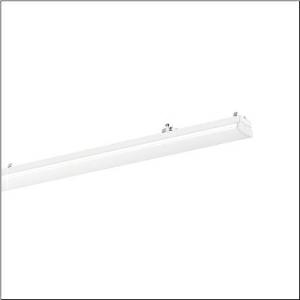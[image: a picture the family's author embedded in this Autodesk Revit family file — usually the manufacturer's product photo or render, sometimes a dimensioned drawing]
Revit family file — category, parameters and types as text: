
# Revit family: licross_21_recessed_opal_mo_52tl1ddn445g
name_source: partatom
category: Lighting Fixtures
units: mm (PartAtom-declared; Revit-internal decimal feet)

## family parameters
Cut with Voids When Loaded = No
Host = Face
Light Source = No
Part Type = Normal
Room Calculation Point = No
Round Connector Dimension = Use Diameter
Shared = No

## types (1)
- --- (1 x LED, 4500 lm, 25.8 W, 4000K)
    Apparent Load = 26 VA
    CIE Flux Codes = 44 73 91 87 100
    Color Rendering = 80
    Color Temperature = 4000K
    Default Elevation = 1800 mm
    Description = Licross 21 recessed opal MO, luminaire insert, of sheet steel, galvanised, coil coated, white, length: 1.500mm, width: 66mm, height: 67mm, LED rated luminous flux: 4.500lm, light colour: 840, SDCM (Standard Deviation of Colour Matching)MacAdam ≤ 3 SDCM (initial), control gear: DALI 2, with plug, 5-pole, with phase selection, mains connection: 220..240V, AC, 50/60Hz, rated input power: 26W, internal wiring halogen-free, primary optical cover: cover, of PMMA, light emission: direct with ceiling illumination distribution, primary light characteristic: symmetric, protection rating (complete): IP40, insulation class (complete): insulation class I (protective earthing), certification: CE, ENEC, VDE, UKCA, protection symbol: D if used in an environment without relevant dust loads with corresponding accessories, impact resistance: IK06, permissible ambient temperature for indoor applications: -25..+45°C, corresponds to IFS (International Featured Standards) requirements for safety and quality in the food industry, reducing of maximum allowable ambient temperature of 5°C with ceiling mounting, LABS conformity tested according to VDMA 24364:2018-05, The light source and the operating device comply with the requirements of the Ecodesign Regulation (EU) 2019/2020 and are replaceable in accordance with this regulation, packaging unit: 1 piece
    Height = 83 mm
    Lamp = 1 x LED
    Lamp Light Flux = 4500 lm
    Lamp Power = 25.8 W
    Lamp count = 1
    Length = 1500 mm
    Luminous efficacy = 174 lm/W
    Manufacturer = Siteco
    ModVariant = No
    Model = 52TL1DDN445G
    Mounting Place = Ceiling
    Mounting Type = Pendant
    Number of Poles = 1
    OnlyDefault = Yes
    Power Factor = 1
    Product Name = Licross 21 recessed opal MO
    Product group = luminaire insert | ceiling pendant
    ProductGroupID = 901
    Protection Class = Protection class I
    Protection Degree = IP 40
    RLX_Detail_Level = 1
    RLX_Emergency_Light_Flux = 0 lm
    RLX_Emergency_Type = 0
    RLX_Emergency_Type_DB = No
    RlxData = <blob elided: 26677 chars, md5=c213cbc9>
    Socket = socket
    Standby Power = 0 W
    System Light Flux = 4500 lm
    System Power = 26 W
    Type Comments = factory setting: luminous flux: 100 % | dim-lin: 254 | 172 mA
    Type Image = l_1313666.jpg
    URL = http://relux.com
    VarID = @adj_070803
    Voltage = 0 V
    Weight = 0.00 kg
    Width = 76 mm

## geometry (parser evidence)
native form markers: Blend x4, Sweep x12
no freeform markers — native parametric forms only
